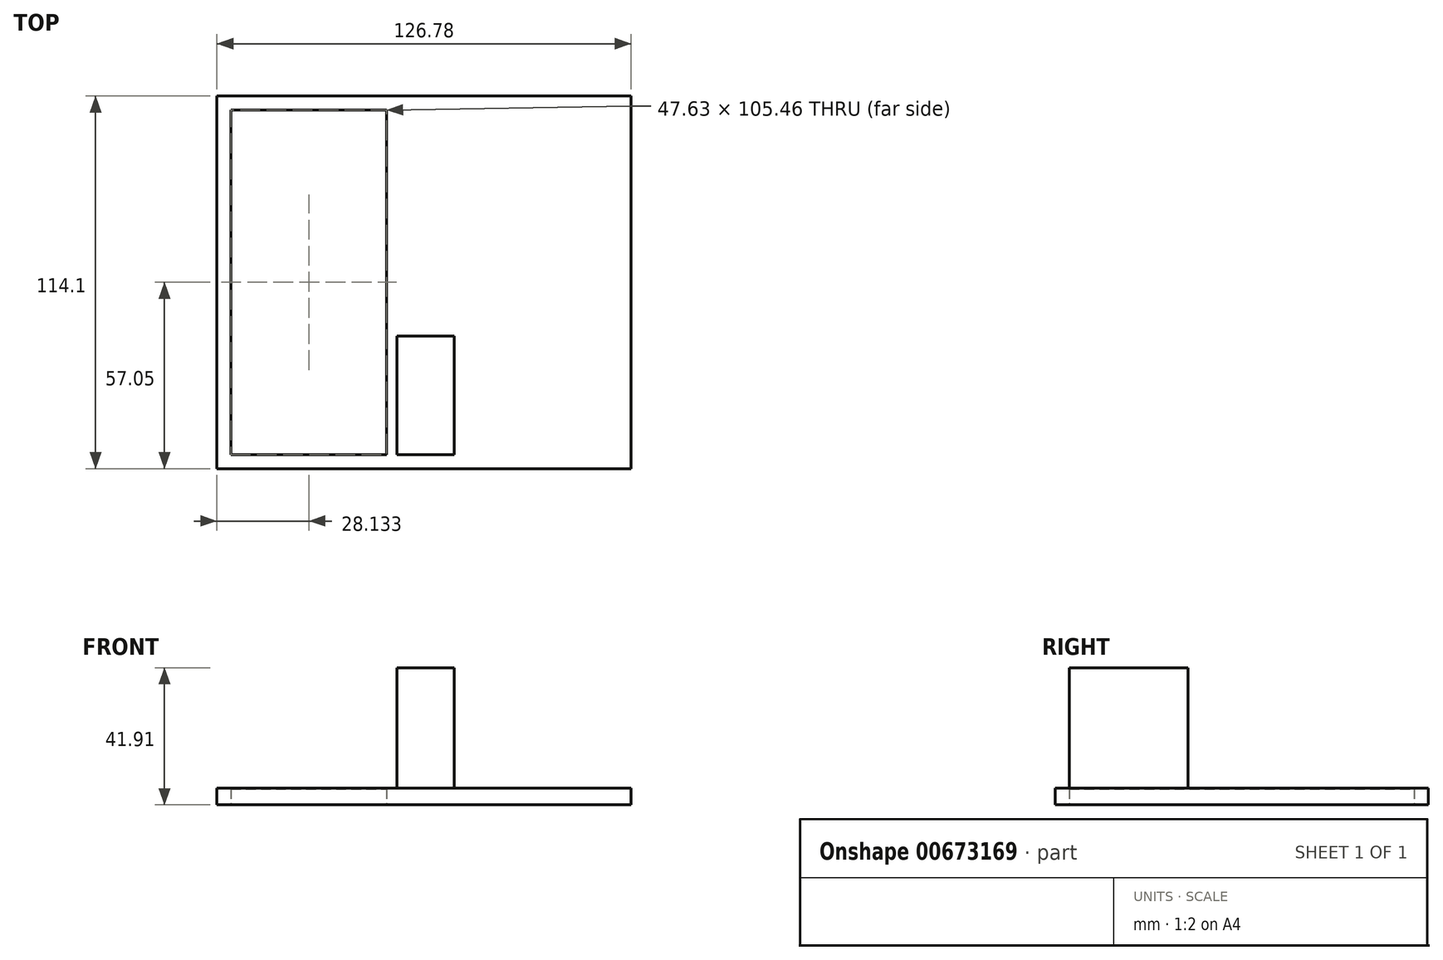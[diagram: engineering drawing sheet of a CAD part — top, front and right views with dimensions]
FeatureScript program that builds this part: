
annotation { "Feature Type Name" : "Feature", "Feature Type Description" : "" }
export const myFeature = defineFeature(function(context is Context, id is Id, definition is map)
    precondition{}
    {
        {
            var Q0;
            Q0=qCreatedBy(makeId("Top.planeOp"),FACE);
            var sketch = newSketch(context, id + "F0", { "sketchPlane" : qUnion([Q0])});
            skLineSegment(sketch, "E0.bottom", {"start": v(-63.39, -57.05) * mm, "end": v(63.39, -57.05) * mm});
            skLineSegment(sketch, "E0.top", {"start": v(-63.39, 57.05) * mm, "end": v(63.39, 57.05) * mm});
            skLineSegment(sketch, "E0.left", {"start": v(-63.39, -57.05) * mm, "end": v(-63.39, 57.05) * mm});
            skLineSegment(sketch, "E0.right", {"start": v(63.39, -57.05) * mm, "end": v(63.39, 57.05) * mm});
            skPoint(sketch, "E0.middle", {"position": v(0, 0) * mm});
            skLineSegment(sketch, "E1.0", {"start": v(9.23, -52.73) * mm, "end": v(9.23, -16.4) * mm});
            skLineSegment(sketch, "E2.trimOffspring", {"start": v(-8.27, -52.73) * mm, "end": v(9.23, -52.73) * mm});
            skLineSegment(sketch, "E3.0", {"start": v(-8.27, -52.73) * mm, "end": v(-8.27, -16.4) * mm});
            skLineSegment(sketch, "E4.0", {"start": v(-59.07, -52.73) * mm, "end": v(-59.07, 52.73) * mm});
            skLineSegment(sketch, "E5.0", {"start": v(-59.07, -52.73) * mm, "end": v(-11.44, -52.73) * mm});
            skLineSegment(sketch, "E6.0", {"start": v(-59.07, 52.73) * mm, "end": v(-11.44, 52.73) * mm});
            skLineSegment(sketch, "E7.0", {"start": v(-11.44, -52.73) * mm, "end": v(-11.44, 52.73) * mm});
            skLineSegment(sketch, "E8.trimOffspring", {"start": v(-8.27, -16.4) * mm, "end": v(9.23, -16.4) * mm});
            skLineSegment(sketch, "E9.0", {"start": v(-55.9, -49.56) * mm, "end": v(-55.9, 49.56) * mm});
            skLineSegment(sketch, "E10.0", {"start": v(-55.9, -49.56) * mm, "end": v(-14.62, -49.56) * mm});
            skLineSegment(sketch, "E11.0", {"start": v(-14.62, -49.56) * mm, "end": v(-14.62, 49.56) * mm});
            skLineSegment(sketch, "E12.0", {"start": v(-55.9, 49.56) * mm, "end": v(-14.62, 49.56) * mm});
            skSolve(sketch);
        }
        {
            var Q0;
            Q0=makeQuery(id+"F0.imprint","IMPRINT",FACE,{"disambiguationData":[TD([[makeQuery(id+"F0.imprint","IMPRINT",EDGE,{"derivedFrom":sQuery(id+"F0.wireOp",EDGE,"E1.0")}),1.0]])]});
            extrude(context, id + "F1", {"entities" : qUnion([Q0]), "depth" : 41.9 * mm, "offsetDistance" : 25.4 * mm});
        }
        {
            var Q0;
            Q0=makeQuery(id+"F0.imprint","IMPRINT",FACE,{"disambiguationData":[TD([[makeQuery(id+"F0.imprint","IMPRINT",EDGE,{"derivedFrom":sQuery(id+"F0.wireOp",EDGE,"E0.bottom")}),1.0]])]});
            extrude(context, id + "F2", {"entities" : qUnion([Q0]), "operationType" : NewBodyOperationType.ADD, "depth" : 5.08 * mm, "offsetDistance" : 25.4 * mm});
        }
        {
            var Q0;
            Q0=makeQuery(id+"F0.imprint","IMPRINT",FACE,{"disambiguationData":[TD([[makeQuery(id+"F0.imprint","IMPRINT",EDGE,{"derivedFrom":sQuery(id+"F0.wireOp",EDGE,"E9.0")}),-1.0]])]});
            extrude(context, id + "F3", {"entities" : qUnion([Q0]), "operationType" : NewBodyOperationType.REMOVE, "endBound" : BoundingType.THROUGH_ALL, "depth" : 25.4 * mm, "offsetDistance" : 25.4 * mm});
        }
        {
            var Q0;
            Q0=makeQuery(id+"F0.imprint","IMPRINT",FACE,{"disambiguationData":[TD([[makeQuery(id+"F0.imprint","IMPRINT",EDGE,{"derivedFrom":sQuery(id+"F0.wireOp",EDGE,"E4.0")}),-1.0]])]});
            var Q1;
            Q1=makeQuery(id+"F0.imprint","IMPRINT",FACE,{"disambiguationData":[TD([[makeQuery(id+"F0.imprint","IMPRINT",EDGE,{"derivedFrom":sQuery(id+"F0.wireOp",EDGE,"E9.0")}),-1.0]])]});
            extrude(context, id + "F4", {"entities" : qUnion([Q0, Q1]), "depth" : 4.76 * mm, "offsetDistance" : 25.4 * mm});
        }
    });
